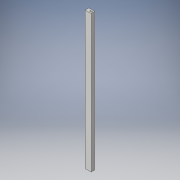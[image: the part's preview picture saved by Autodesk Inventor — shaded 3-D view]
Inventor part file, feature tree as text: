
AUTODESK INVENTOR PART (.ipt)
format: ipt  version: 2017 (Build 210142000, 142)  size: 102,400 bytes
history: native  units: in
note: dims shown in document units (in); Inventor stores cm internally (conversion verified against a paired STEP export)
features: extrude x1, sketch x1
ambient origin geometry x8: Origin, YZ Plane, XZ Plane, XY Plane, X Axis, Y Axis, Z Axis, Center Point
bodies: Solid1 (feature_tree)
feature tree (2):
  extrude  "Extrusion1"  Depth=0.25in
  sketch  "Sketch1"  dims[d0=1.0in d1=0.25in d2=0.5in d3=0.125in d4=1.0in d5=0.25in d6=23.0in d7=0.0in]
